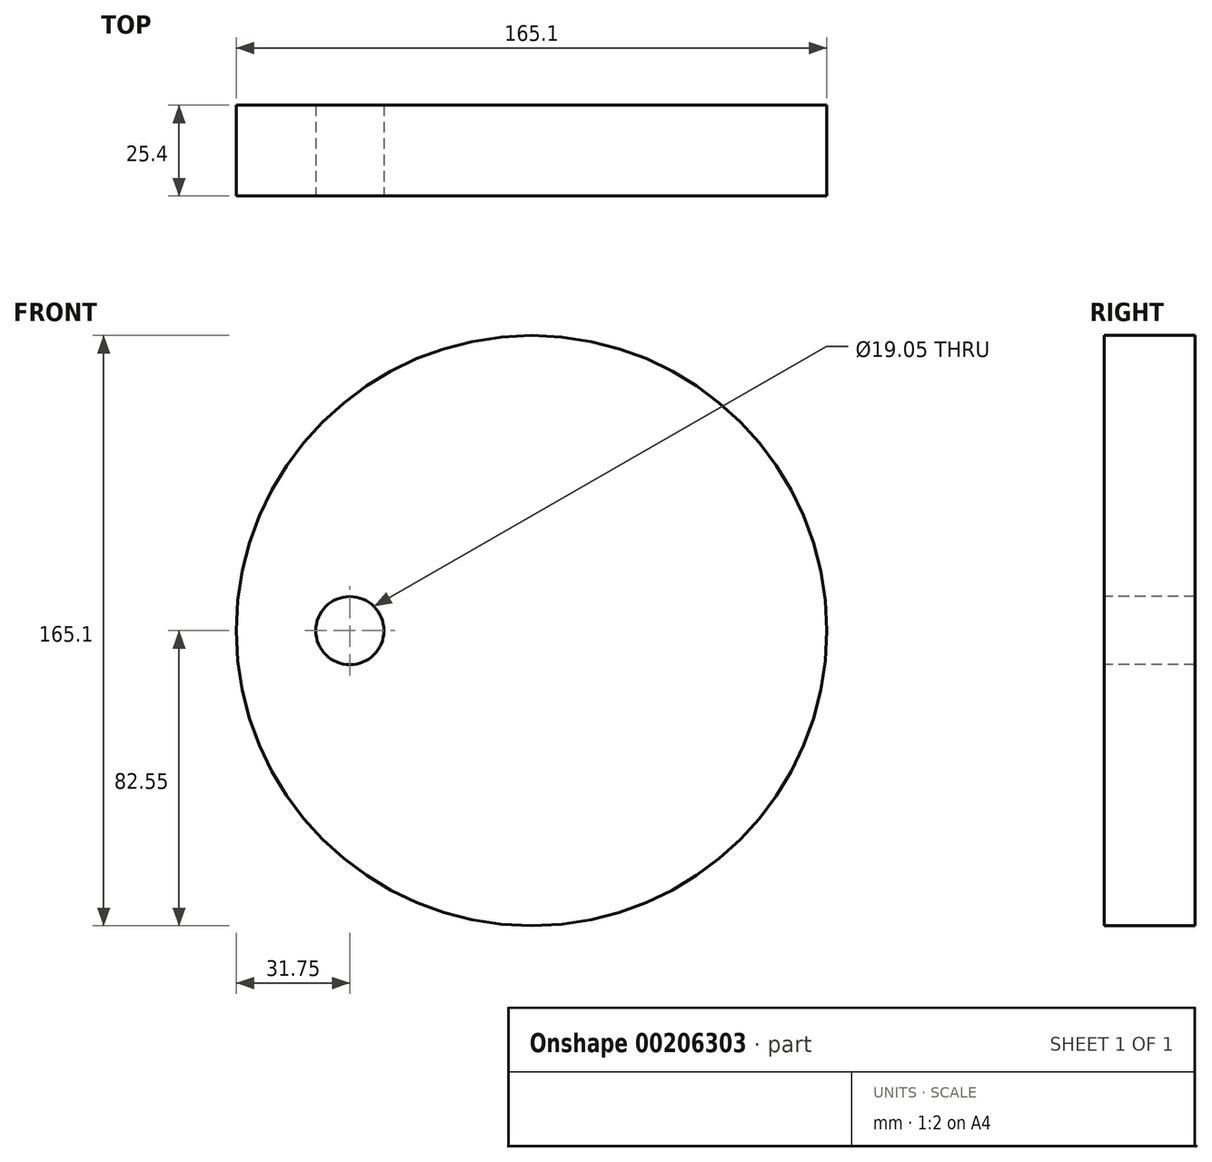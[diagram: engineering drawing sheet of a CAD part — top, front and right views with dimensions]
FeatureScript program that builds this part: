
annotation { "Feature Type Name" : "Feature", "Feature Type Description" : "" }
export const myFeature = defineFeature(function(context is Context, id is Id, definition is map)
    precondition{}
    {
        {
            var Q0;
            Q0=qCreatedBy(makeId("Front.planeOp"),FACE);
            var sketch = newSketch(context, id + "F0", { "sketchPlane" : qUnion([Q0])});
            skCircle(sketch, "E0", {"center": v(0, 0) * mm, "radius": 133.35 * mm, "construction": true});
            skCircle(sketch, "E1", {"center": v(0, 0) * mm, "radius": 31.75 * mm, "construction": true});
            skCircle(sketch, "E2", {"center": v(50.8, 0) * mm, "radius": 82.55 * mm});
            skCircle(sketch, "E3", {"center": v(0, 0) * mm, "radius": 9.53 * mm});
            skSolve(sketch);
        }
        {
            var Q0;
            Q0=makeQuery(id+"F0.imprint","IMPRINT",FACE,{"disambiguationData":[TD([[makeQuery(id+"F0.imprint","IMPRINT",EDGE,{"derivedFrom":sQuery(id+"F0.wireOp",EDGE,"E2")}),1.0]])]});
            extrude(context, id + "F1", {"entities" : qUnion([Q0]), "oppositeDirection" : true, "depth" : 25.4 * mm});
        }
    });
